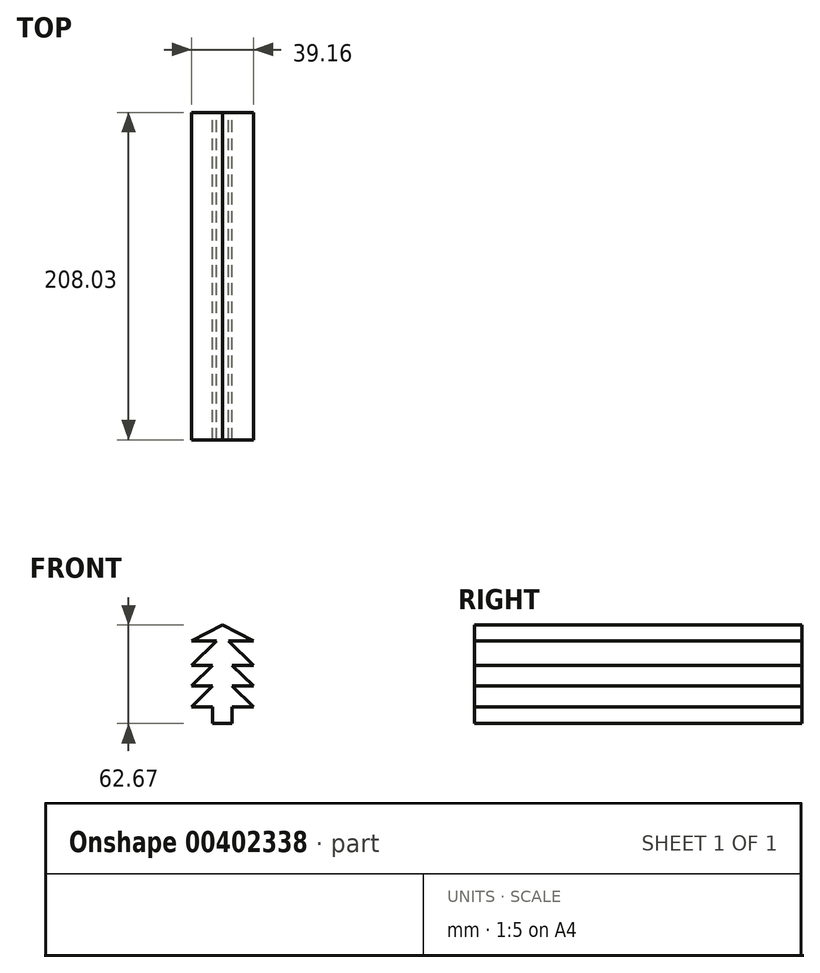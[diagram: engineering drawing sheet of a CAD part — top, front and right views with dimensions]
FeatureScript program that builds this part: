
annotation { "Feature Type Name" : "Feature", "Feature Type Description" : "" }
export const myFeature = defineFeature(function(context is Context, id is Id, definition is map)
    precondition{}
    {
        {
            var Q0;
            Q0=qCreatedBy(makeId("Front.planeOp"),FACE);
            var sketch = newSketch(context, id + "F0", { "sketchPlane" : qUnion([Q0])});
            skLineSegment(sketch, "E0", {"start": v(0, 55.58) * mm, "end": v(-19.58, 45.32) * mm});
            skLineSegment(sketch, "E1", {"start": v(-19.58, 45.32) * mm, "end": v(-3.73, 45.32) * mm});
            skLineSegment(sketch, "E2", {"start": v(-3.73, 45.32) * mm, "end": v(-19.58, 29.84) * mm});
            skLineSegment(sketch, "E3", {"start": v(-19.58, 29.84) * mm, "end": v(-6.15, 29.84) * mm});
            skLineSegment(sketch, "E4", {"start": v(-6.15, 29.84) * mm, "end": v(-19.58, 16.73) * mm});
            skLineSegment(sketch, "E5", {"start": v(-19.58, 16.73) * mm, "end": v(-6.15, 16.73) * mm});
            skLineSegment(sketch, "E6", {"start": v(-6.15, 16.73) * mm, "end": v(-19.58, 3.62) * mm});
            skLineSegment(sketch, "E7", {"start": v(-19.58, 3.62) * mm, "end": v(-6.15, 3.62) * mm});
            skLineSegment(sketch, "E8", {"start": v(-6.15, 3.62) * mm, "end": v(-6.15, -7.09) * mm});
            skLineSegment(sketch, "E9", {"start": v(-6.15, -7.09) * mm, "end": v(0, -7.09) * mm});
            skLineSegment(sketch, "E10.MirrorCS", {"start": v(0, 55.58) * mm, "end": v(19.58, 45.32) * mm});
            skLineSegment(sketch, "E11.MirrorCS", {"start": v(19.58, 45.32) * mm, "end": v(3.73, 45.32) * mm});
            skLineSegment(sketch, "E12.MirrorCS", {"start": v(3.73, 45.32) * mm, "end": v(19.58, 29.84) * mm});
            skLineSegment(sketch, "E13.MirrorCS", {"start": v(19.58, 29.84) * mm, "end": v(6.15, 29.84) * mm});
            skLineSegment(sketch, "E14.MirrorCS", {"start": v(6.15, 29.84) * mm, "end": v(19.58, 16.73) * mm});
            skLineSegment(sketch, "E15.MirrorCS", {"start": v(19.58, 16.73) * mm, "end": v(6.15, 16.73) * mm});
            skLineSegment(sketch, "E16.MirrorCS", {"start": v(6.15, 16.73) * mm, "end": v(19.58, 3.62) * mm});
            skLineSegment(sketch, "E17.MirrorCS", {"start": v(19.58, 3.62) * mm, "end": v(6.15, 3.62) * mm});
            skLineSegment(sketch, "E18.MirrorCS", {"start": v(6.15, -7.09) * mm, "end": v(0, -7.09) * mm});
            skLineSegment(sketch, "E19.MirrorCS", {"start": v(6.15, 3.62) * mm, "end": v(6.15, -7.09) * mm});
            skSolve(sketch);
        }
        {
            var Q0;
            Q0=makeQuery(id+"F0.imprint","IMPRINT",FACE,{"disambiguationData":[TD([[makeQuery(id+"F0.imprint","IMPRINT",EDGE,{"derivedFrom":sQuery(id+"F0.wireOp",EDGE,"E0")}),1.0]])]});
            extrude(context, id + "F1", {"entities" : qUnion([Q0]), "depth" : 208.03 * mm});
        }
    });
